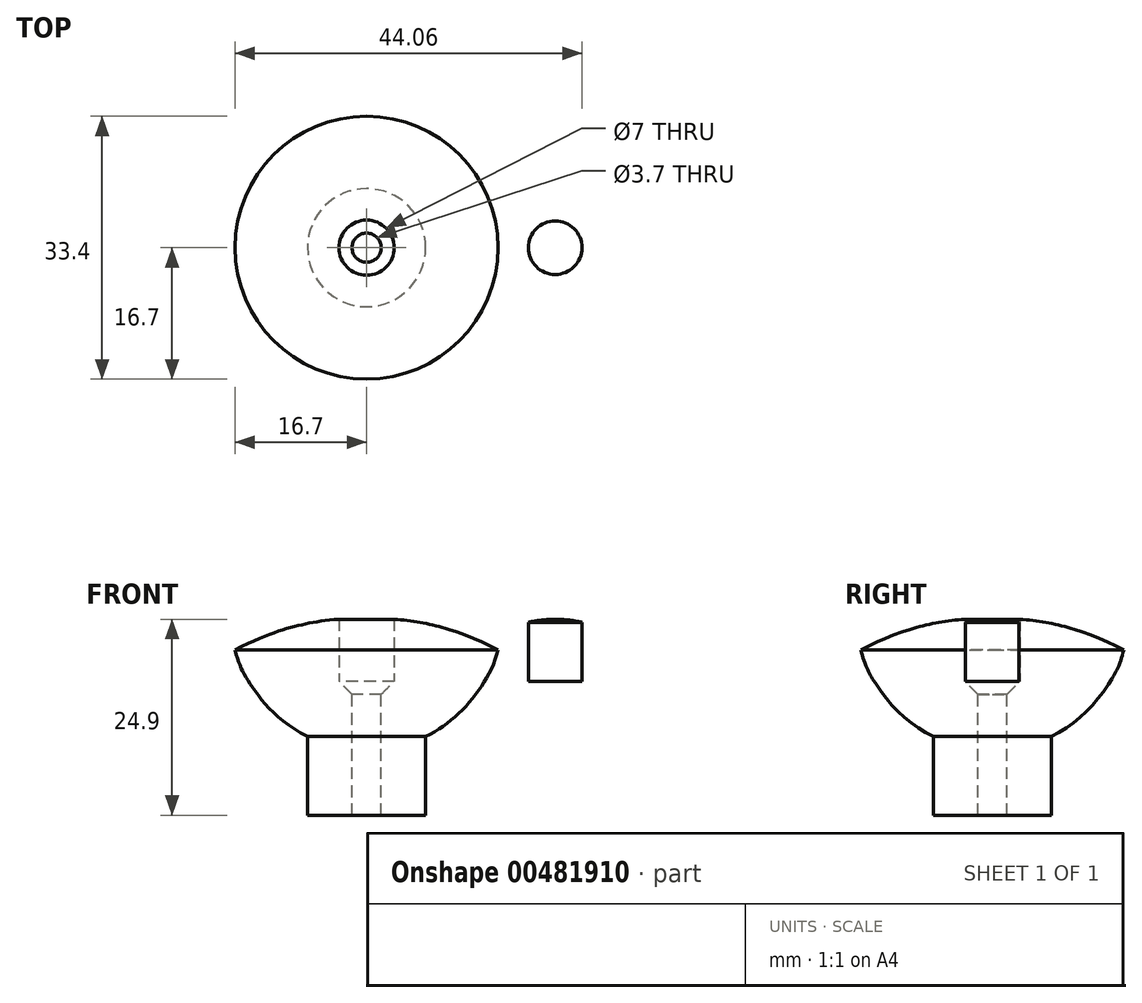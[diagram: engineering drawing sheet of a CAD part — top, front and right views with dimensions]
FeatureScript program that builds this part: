
annotation { "Feature Type Name" : "Feature", "Feature Type Description" : "" }
export const myFeature = defineFeature(function(context is Context, id is Id, definition is map)
    precondition{}
    {
        {
            var Q0;
            Q0=qCreatedBy(makeId("Front.planeOp"),FACE);
            var sketch = newSketch(context, id + "F0", { "sketchPlane" : qUnion([Q0])});
            skLineSegment(sketch, "E0", {"start": v(0, 0) * mm, "end": v(0, 25) * mm});
            skLineSegment(sketch, "E1", {"start": v(0, 0) * mm, "end": v(7.5, 0) * mm});
            skLineSegment(sketch, "E2", {"start": v(7.5, 0) * mm, "end": v(7.5, 10) * mm});
            skFitSpline(sketch, "E3", {"points": [v(7.5, 10) * mm, v(15.09, 17.17) * mm, v(16.7, 21) * mm], "startDerivative": vector(20.41, 10.3) * mm, "endDerivative": vector(3.52, 13.62) * mm});
            skFitSpline(sketch, "E4", {"points": [v(0, 25) * mm, v(8.15, 24.22) * mm, v(16.7, 21) * mm], "startDerivative": vector(24.92, 0) * mm, "endDerivative": vector(24, -12.13) * mm});
            skSolve(sketch);
        }
        {
            var Q0;
            Q0=makeQuery(id+"F0.imprint","IMPRINT",FACE,{"disambiguationData":[TD([[makeQuery(id+"F0.imprint","IMPRINT",EDGE,{"derivedFrom":sQuery(id+"F0.wireOp",EDGE,"E0")}),-1.0]])]});
            var Q1;
            Q1=sQuery(id+"F0.wireOp",EDGE,"E0");
            revolve(context, id + "F1", {"entities" : qUnion([Q0]), "axis" : qUnion([Q1]), "revolveType" : RevolveType.FULL});
        }
        {
            var Q0;
            Q0=makeQuery(id+"F1.opRevolve","SWEPT_FACE",FACE,{"disambiguationData":[OSD([sQuery(id+"F0.wireOp",EDGE,"E1")])]});
            cPlane(context, id + "F2", {"entities" : qUnion([Q0]), "cplaneType" : CPlaneType.OFFSET, "offset" : 17 * mm, "oppositeDirection" : true, "width" : 150 * mm, "height" : 150 * mm});
        }
        {
            var Q0;
            Q0=qCreatedBy(id+"F2.planeOp",FACE);
            var sketch = newSketch(context, id + "F3", { "sketchPlane" : qUnion([Q0])});
            skPoint(sketch, "E5", {"position": v(0, 0) * mm});
            skSolve(sketch);
        }
        {
            var Q0;
            Q0=sQuery(id+"F3.wireOp",VERTEX,"E5");
            var Q1;
            Q1=makeQuery(id+"F1.opRevolve","SWEPT_BODY",BODY,{"disambiguationData":[OSD([sQuery(id+"F0.wireOp",EDGE,"E0"),sQuery(id+"F0.wireOp",EDGE,"E1"),sQuery(id+"F0.wireOp",EDGE,"E2"),sQuery(id+"F0.wireOp",EDGE,"E3"),sQuery(id+"F0.wireOp",EDGE,"E4")])]});
            hole(context, id + "F4", {"style" : HoleStyle.SIMPLE, "endStyle" : HoleEndStyle.THROUGH, "holeDiameter" : 7 * mm, "isTappedThrough" : true, "tappedDepth" : 12 * mm, "tapClearance" : 3, "locations" : qUnion([Q0]), "scope" : qUnion([Q1])});
        }
        {
            var Q0;
            Q0=sQuery(id+"F3.wireOp",VERTEX,"E5");
            var Q1;
            Q1=makeQuery(id+"F1.opRevolve","SWEPT_BODY",BODY,{"disambiguationData":[OSD([sQuery(id+"F0.wireOp",EDGE,"E0"),sQuery(id+"F0.wireOp",EDGE,"E1"),sQuery(id+"F0.wireOp",EDGE,"E2"),sQuery(id+"F0.wireOp",EDGE,"E3"),sQuery(id+"F0.wireOp",EDGE,"E4")])]});
            hole(context, id + "F5", {"style" : HoleStyle.C_SINK, "endStyle" : HoleEndStyle.THROUGH, "oppositeDirection" : true, "holeDiameter" : 3.7 * mm, "cSinkDiameter" : 7 * mm, "cSinkAngle" : 90 * degree, "isTappedThrough" : true, "tappedDepth" : 12 * mm, "tapClearance" : 3, "locations" : qUnion([Q0]), "scope" : qUnion([Q1])});
        }
        {
            var Q0;
            Q0=qCreatedBy(makeId("Front.planeOp"),FACE);
            var sketch = newSketch(context, id + "F6", { "sketchPlane" : qUnion([Q0])});
            skLineSegment(sketch, "E6", {"start": v(20.56, 24.5) * mm, "end": v(20.56, 17) * mm});
            skLineSegment(sketch, "E7", {"start": v(20.56, 17) * mm, "end": v(27.36, 17) * mm});
            skLineSegment(sketch, "E8", {"start": v(27.36, 17) * mm, "end": v(27.36, 24.5) * mm});
            skPoint(sketch, "E9", {"position": v(23.96, 17) * mm});
            skLineSegment(sketch, "E10", {"start": v(23.96, 17) * mm, "end": v(23.96, 30.96) * mm});
            skFitSpline(sketch, "E11", {"points": [v(20.56, 24.5) * mm, v(27.36, 24.5) * mm], "startDerivative": vector(6.26, 1.53) * mm, "endDerivative": vector(6.4, -1.53) * mm});
            skSolve(sketch);
        }
        {
            var Q0;
            Q0=makeQuery(id+"F6.imprint","IMPRINT",FACE,{"disambiguationData":[TD([[makeQuery(id+"F6.imprint","IMPRINT",EDGE,{"derivedFrom":sQuery(id+"F6.wireOp",EDGE,"E6")}),1.0]])]});
            var Q1;
            Q1=sQuery(id+"F6.wireOp",EDGE,"E10");
            revolve(context, id + "F7", {"entities" : qUnion([Q0]), "axis" : qUnion([Q1]), "revolveType" : RevolveType.FULL});
        }
    });
